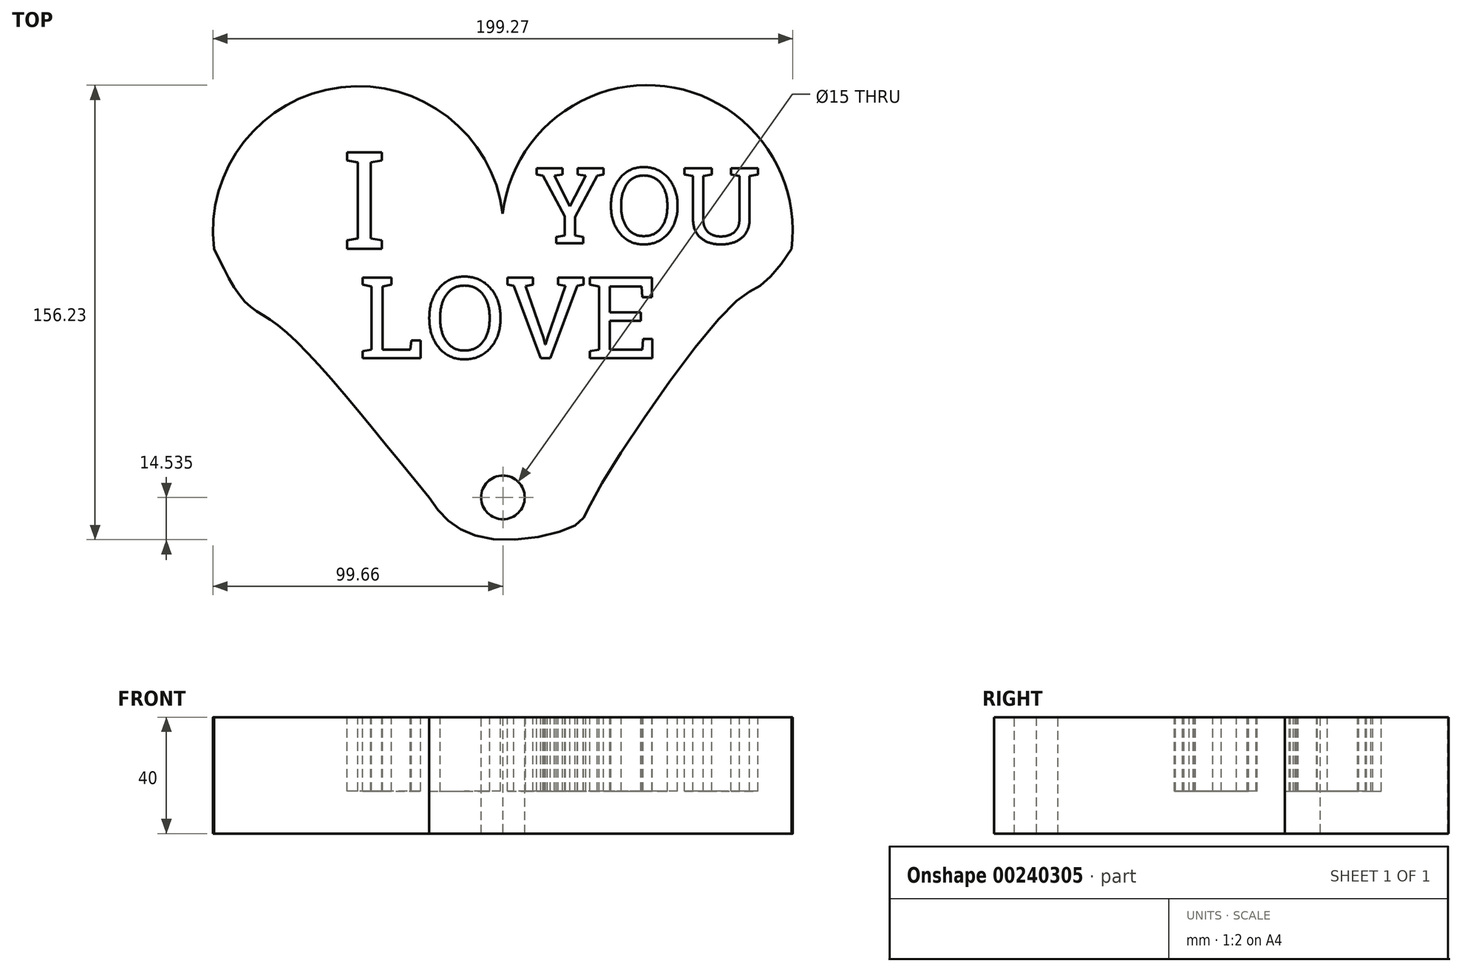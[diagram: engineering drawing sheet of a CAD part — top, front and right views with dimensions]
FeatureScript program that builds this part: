
annotation { "Feature Type Name" : "Feature", "Feature Type Description" : "" }
export const myFeature = defineFeature(function(context is Context, id is Id, definition is map)
    precondition{}
    {
        {
            var Q0;
            Q0=qCreatedBy(makeId("Top.planeOp"),FACE);
            var sketch = newSketch(context, id + "F0", { "sketchPlane" : qUnion([Q0])});
            skLineSegment(sketch, "E0", {"start": v(0, 0) * mm, "end": v(-50, 0) * mm, "construction": true});
            skLineSegment(sketch, "E1", {"start": v(0, 0) * mm, "end": v(50, 0) * mm, "construction": true});
            skLineSegment(sketch, "E2", {"start": v(-50, 0) * mm, "end": v(-99.31, 0) * mm, "construction": true});
            skLineSegment(sketch, "E3", {"start": v(99.22, 0) * mm, "end": v(50, 0) * mm, "construction": true});
            skPoint(sketch, "E4.second.point", {"position": v(0, 3.18) * mm});
            skPoint(sketch, "E4.third.point", {"position": v(-61.4, -46.94) * mm});
            skArc(sketch, "E5", {"start": v(99.22, 0) * mm, "mid": v(49.61, 56.22) * mm, "end": v(0, 0) * mm});
            skPoint(sketch, "E5.third.point", {"position": v(32.84, -40.88) * mm});
            skArc(sketch, "E6", {"start": v(0, 0) * mm, "mid": v(-49.66, 55.86) * mm, "end": v(-99.31, 0) * mm});
            skPoint(sketch, "E6.third.point", {"position": v(-13.86, 40.77) * mm});
            skLineSegment(sketch, "E7", {"start": v(0, 0) * mm, "end": v(0, -100) * mm, "construction": true});
            skFitSpline(sketch, "E8", {"points": [v(-99.31, 0) * mm, v(-88.32, -18.55) * mm, v(-76.52, -26.9) * mm, v(-25.42, -85.48) * mm], "startDerivative": vector(39.18, -80.81) * mm, "endDerivative": vector(116.23, -142.46) * mm});
            skFitSpline(sketch, "E9", {"points": [v(-25.42, -85.48) * mm, v(-16.57, -95.21) * mm, v(0, -100) * mm, v(24.7, -95.21) * mm, v(31.28, -85.48) * mm, v(78.84, -19.22) * mm, v(89.08, -12.16) * mm, v(99.22, 0) * mm], "startDerivative": vector(69.06, -107.53) * mm, "endDerivative": vector(79.24, 125.22) * mm});
            skSolve(sketch);
        }
        {
            var Q0;
            Q0 = qSketchRegion(id + "F0", true);
            extrude(context, id + "F1", {"entities" : qUnion([Q0]), "depth" : 40 * mm});
        }
        {
            var Q0;
            Q0=makeQuery(id+"F1.opExtrude","CAP_FACE",FACE,{"disambiguationData":[OSD([sQuery(id+"F0.wireOp",EDGE,"E5"),sQuery(id+"F0.wireOp",EDGE,"E6"),sQuery(id+"F0.wireOp",EDGE,"E8"),sQuery(id+"F0.wireOp",EDGE,"E9")])],"isStart":false});
            var sketch = newSketch(context, id + "F2", { "sketchPlane" : qUnion([Q0])});
            skText(sketch, "E10", { "text": "I", "fontName": "RobotoSlab-Regular.ttf"});
            skText(sketch, "E11", { "text": "LOVE", "fontName": "RobotoSlab-Regular.ttf"});
            skText(sketch, "E12", { "text": "YOU", "fontName": "RobotoSlab-Regular.ttf"});
            const initialGuessF2  = {"E10": [-0.05518, 0, 1, 0, 0.03359], "E11": [-0.04959, -0.03764, 1, 0, 0.02802], "E12": [0.01061, 0.00186, 1, 0, 0.02617]};
            skSetInitialGuess(sketch, initialGuessF2);
            skSolve(sketch);
        }
        {
            var Q0;
            Q0 = qSketchRegion(id + "F2", true);
            extrude(context, id + "F3", {"entities" : qUnion([Q0]), "operationType" : NewBodyOperationType.REMOVE, "oppositeDirection" : true, "depth" : 25.4 * mm});
        }
        {
            var Q0;
            {var subQ0=sQuery(id+"F0.wireOp",EDGE,"E8");var subQ1=sQuery(id+"F0.wireOp",EDGE,"E5");var subQ2=sQuery(id+"F0.wireOp",EDGE,"E9");var subQ3=sQuery(id+"F0.wireOp",EDGE,"E6");Q0=makeQuery(id+"F3.boolean.opBoolean","SPLIT",FACE,{"disambiguationData":[TD([makeQuery(id+"F1.opExtrude","SWEPT_FACE",FACE,{"disambiguationData":[OSD([subQ1])]})])],"derivedFrom":makeQuery(id+"F1.opExtrude","CAP_FACE",FACE,{"disambiguationData":[OSD([subQ1,subQ3,subQ0,subQ2])],"isStart":false})});}
            var sketch = newSketch(context, id + "F4", { "sketchPlane" : qUnion([Q0])});
            skLineSegment(sketch, "E13", {"start": v(-25.42, -85.48) * mm, "end": v(31.28, -85.48) * mm, "construction": true});
            skLineSegment(sketch, "E14", {"start": v(0, -100) * mm, "end": v(0, -85.48) * mm, "construction": true});
            skCircle(sketch, "E15", {"center": v(0, -85.48) * mm, "radius": 7.5 * mm});
            skSolve(sketch);
        }
        {
            var Q0;
            Q0=makeQuery(id+"F4.imprint","IMPRINT",FACE,{"disambiguationData":[TD([[makeQuery(id+"F4.imprint","IMPRINT",EDGE,{"derivedFrom":sQuery(id+"F4.wireOp",EDGE,"E15")}),1.0]])]});
            extrude(context, id + "F5", {"entities" : qUnion([Q0]), "operationType" : NewBodyOperationType.REMOVE, "oppositeDirection" : true, "depth" : 70.36 * mm});
        }
    });
